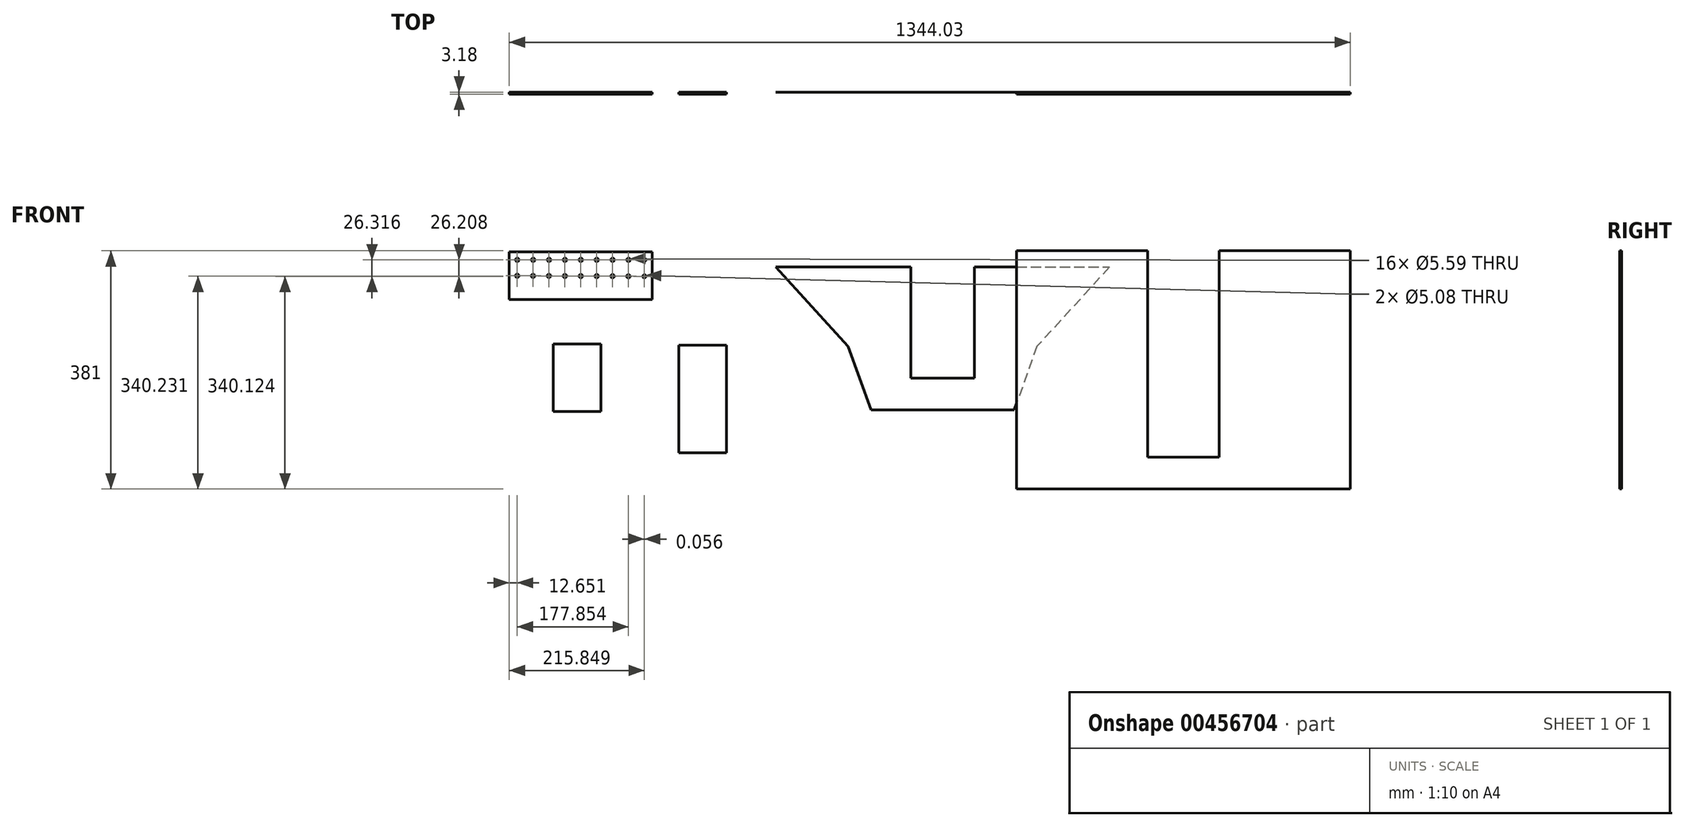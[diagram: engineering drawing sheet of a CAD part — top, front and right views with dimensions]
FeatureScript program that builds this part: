
annotation { "Feature Type Name" : "Feature", "Feature Type Description" : "" }
export const myFeature = defineFeature(function(context is Context, id is Id, definition is map)
    precondition{}
    {
        {
            var Q0;
            Q0=qCreatedBy(makeId("Front.planeOp"),FACE);
            var sketch = newSketch(context, id + "F0", { "sketchPlane" : qUnion([Q0])});
            skLineSegment(sketch, "E0", {"start": v(-433.28, 143.89) * mm, "end": v(100.12, 143.89) * mm});
            skLineSegment(sketch, "E1", {"start": v(-433.28, 143.89) * mm, "end": v(-317.41, 16.89) * mm});
            skLineSegment(sketch, "E2", {"start": v(100.12, 143.89) * mm, "end": v(-15.75, 16.89) * mm});
            skLineSegment(sketch, "E3", {"start": v(-317.41, 16.89) * mm, "end": v(-280.88, -84.71) * mm});
            skLineSegment(sketch, "E4", {"start": v(-15.75, 16.89) * mm, "end": v(-52.28, -84.71) * mm});
            skLineSegment(sketch, "E5", {"start": v(-52.28, -84.71) * mm, "end": v(-280.88, -84.71) * mm});
            skPoint(sketch, "E6", {"position": v(-166.58, 143.89) * mm});
            skLineSegment(sketch, "E7", {"start": v(-217.38, 143.89) * mm, "end": v(-115.78, 143.89) * mm});
            skLineSegment(sketch, "E8", {"start": v(-217.38, 143.89) * mm, "end": v(-217.38, -33.91) * mm});
            skLineSegment(sketch, "E9", {"start": v(-217.38, -33.91) * mm, "end": v(-115.78, -33.91) * mm});
            skLineSegment(sketch, "E10", {"start": v(-115.78, -33.91) * mm, "end": v(-115.78, 143.89) * mm});
            skSolve(sketch);
        }
        {
            var Q0;
            {var subQ1=sQuery(id+"F0.wireOp",EDGE,"E1");Q0=makeQuery(id+"F0.imprint","IMPRINT",FACE,{"disambiguationData":[TD([[makeQuery(id+"F0.imprint","IMPRINT",EDGE,{"derivedFrom":subQ1}),1.0]])]});}
            extrude(context, id + "F1", {"entities" : qUnion([Q0]), "depth" : 1 / 203.2 * mm});
        }
        {
            var Q0;
            Q0=qCreatedBy(makeId("Front.planeOp"),FACE);
            var sketch = newSketch(context, id + "F2", { "sketchPlane" : qUnion([Q0])});
            skLineSegment(sketch, "E11", {"start": v(-48.38, 169.93) * mm, "end": v(-48.38, -211.07) * mm});
            skLineSegment(sketch, "E12", {"start": v(-48.38, -211.07) * mm, "end": v(485.02, -211.07) * mm});
            skLineSegment(sketch, "E13", {"start": v(485.02, 169.93) * mm, "end": v(485.02, -211.07) * mm});
            skLineSegment(sketch, "E14", {"start": v(161.17, 169.93) * mm, "end": v(161.17, -160.27) * mm});
            skLineSegment(sketch, "E15", {"start": v(161.17, -160.27) * mm, "end": v(275.47, -160.27) * mm});
            skLineSegment(sketch, "E16", {"start": v(275.47, -160.27) * mm, "end": v(275.47, 169.93) * mm});
            skLineSegment(sketch, "E17", {"start": v(161.17, 169.93) * mm, "end": v(-48.38, 169.93) * mm});
            skLineSegment(sketch, "E18", {"start": v(275.47, 169.93) * mm, "end": v(485.02, 169.93) * mm});
            skSolve(sketch);
        }
        {
            var Q0;
            Q0=qCreatedBy(makeId("Front.planeOp"),FACE);
            var sketch = newSketch(context, id + "F3", { "sketchPlane" : qUnion([Q0])});
            skLineSegment(sketch, "E19", {"start": v(-859, 168.07) * mm, "end": v(-859, 91.87) * mm});
            skLineSegment(sketch, "E20", {"start": v(-859, 91.87) * mm, "end": v(-630.4, 91.87) * mm});
            skLineSegment(sketch, "E21", {"start": v(-630.4, 91.87) * mm, "end": v(-630.4, 168.07) * mm});
            skLineSegment(sketch, "E22", {"start": v(-630.4, 168.07) * mm, "end": v(-859, 168.07) * mm});
            skLineSegment(sketch, "E23", {"start": v(-859, 155.37) * mm, "end": v(-630.4, 155.37) * mm, "construction": true});
            skLineSegment(sketch, "E24", {"start": v(-859, 129.97) * mm, "end": v(-630.4, 129.97) * mm, "construction": true});
            skPoint(sketch, "E25", {"position": v(-859, 142.67) * mm});
            skCircle(sketch, "E26", {"center": v(-846.3, 155.37) * mm, "radius": 2.8 * mm});
            skCircle(sketch, "E27", {"center": v(-820.9, 155.37) * mm, "radius": 2.8 * mm});
            skCircle(sketch, "E28", {"center": v(-795.5, 155.37) * mm, "radius": 2.8 * mm});
            skCircle(sketch, "E29", {"center": v(-770.1, 155.37) * mm, "radius": 2.8 * mm});
            skCircle(sketch, "E30", {"center": v(-744.7, 155.37) * mm, "radius": 2.8 * mm});
            skCircle(sketch, "E31", {"center": v(-719.3, 155.37) * mm, "radius": 2.8 * mm});
            skCircle(sketch, "E32", {"center": v(-693.9, 155.37) * mm, "radius": 2.8 * mm});
            skCircle(sketch, "E33", {"center": v(-668.5, 155.37) * mm, "radius": 2.8 * mm});
            skCircle(sketch, "E34", {"center": v(-643.1, 155.37) * mm, "radius": 2.54 * mm});
            skLineSegment(sketch, "E35", {"start": v(-630.4, 142.18) * mm, "end": v(-859, 142.67) * mm, "construction": true});
            skCircle(sketch, "E36.MirrorC", {"center": v(-846.36, 129.92) * mm, "radius": 2.8 * mm});
            skCircle(sketch, "E37.MirrorC", {"center": v(-820.96, 129.8) * mm, "radius": 2.8 * mm});
            skCircle(sketch, "E38.MirrorC", {"center": v(-795.56, 129.7) * mm, "radius": 2.8 * mm});
            skCircle(sketch, "E39.MirrorC", {"center": v(-770.16, 129.6) * mm, "radius": 2.8 * mm});
            skCircle(sketch, "E40.MirrorC", {"center": v(-744.76, 129.48) * mm, "radius": 2.8 * mm});
            skCircle(sketch, "E41.MirrorC", {"center": v(-719.36, 129.38) * mm, "radius": 2.8 * mm});
            skCircle(sketch, "E42.MirrorC", {"center": v(-693.96, 129.27) * mm, "radius": 2.8 * mm});
            skCircle(sketch, "E43.MirrorC", {"center": v(-668.56, 129.16) * mm, "radius": 2.8 * mm});
            skCircle(sketch, "E44.MirrorC", {"center": v(-643.16, 129.05) * mm, "radius": 2.54 * mm});
            skSolve(sketch);
        }
        {
            var Q0;
            Q0=qCreatedBy(makeId("Front.planeOp"),FACE);
            var sketch = newSketch(context, id + "F4", { "sketchPlane" : qUnion([Q0])});
            skLineSegment(sketch, "E45.bottom", {"start": v(-712.6, 20.63) * mm, "end": v(-788.8, 20.63) * mm});
            skLineSegment(sketch, "E45.top", {"start": v(-712.6, -87.34) * mm, "end": v(-788.8, -87.34) * mm});
            skLineSegment(sketch, "E45.left", {"start": v(-712.6, 20.63) * mm, "end": v(-712.6, -87.34) * mm});
            skLineSegment(sketch, "E45.right", {"start": v(-788.8, 20.63) * mm, "end": v(-788.8, -87.34) * mm});
            skSolve(sketch);
        }
        {
            var Q0;
            Q0=qCreatedBy(makeId("Front.planeOp"),FACE);
            var sketch = newSketch(context, id + "F5", { "sketchPlane" : qUnion([Q0])});
            skLineSegment(sketch, "E46.bottom", {"start": v(-511.91, 18.8) * mm, "end": v(-588.11, 18.8) * mm});
            skLineSegment(sketch, "E46.top", {"start": v(-511.91, -153.1) * mm, "end": v(-588.11, -153.1) * mm});
            skLineSegment(sketch, "E46.left", {"start": v(-511.91, 18.8) * mm, "end": v(-511.91, -153.1) * mm});
            skLineSegment(sketch, "E46.right", {"start": v(-588.11, 18.8) * mm, "end": v(-588.11, -153.1) * mm});
            skSolve(sketch);
        }
        {
            var Q0;
            Q0=makeQuery(id+"F4.imprint","IMPRINT",FACE,{"disambiguationData":[TD([[makeQuery(id+"F4.imprint","IMPRINT",EDGE,{"derivedFrom":sQuery(id+"F4.wireOp",EDGE,"E45.bottom")}),1.0]])]});
            extrude(context, id + "F6", {"entities" : qUnion([Q0]), "depth" : 3.17 * mm});
        }
        {
            var Q0;
            Q0=makeQuery(id+"F5.imprint","IMPRINT",FACE,{"disambiguationData":[TD([[makeQuery(id+"F5.imprint","IMPRINT",EDGE,{"derivedFrom":sQuery(id+"F5.wireOp",EDGE,"E46.bottom")}),1.0]])]});
            extrude(context, id + "F7", {"entities" : qUnion([Q0]), "depth" : 3.17 * mm});
        }
        {
            var Q0;
            Q0=makeQuery(id+"F3.imprint","IMPRINT",FACE,{"disambiguationData":[TD([[makeQuery(id+"F3.imprint","IMPRINT",EDGE,{"derivedFrom":sQuery(id+"F3.wireOp",EDGE,"E19")}),1.0]])]});
            extrude(context, id + "F8", {"entities" : qUnion([Q0]), "depth" : 3.17 * mm});
        }
        {
            var Q0;
            Q0=makeQuery(id+"F2.imprint","IMPRINT",FACE,{"disambiguationData":[TD([[makeQuery(id+"F2.imprint","IMPRINT",EDGE,{"derivedFrom":sQuery(id+"F2.wireOp",EDGE,"E11")}),1.0]])]});
            extrude(context, id + "F9", {"entities" : qUnion([Q0]), "depth" : 3.17 * mm});
        }
    });
